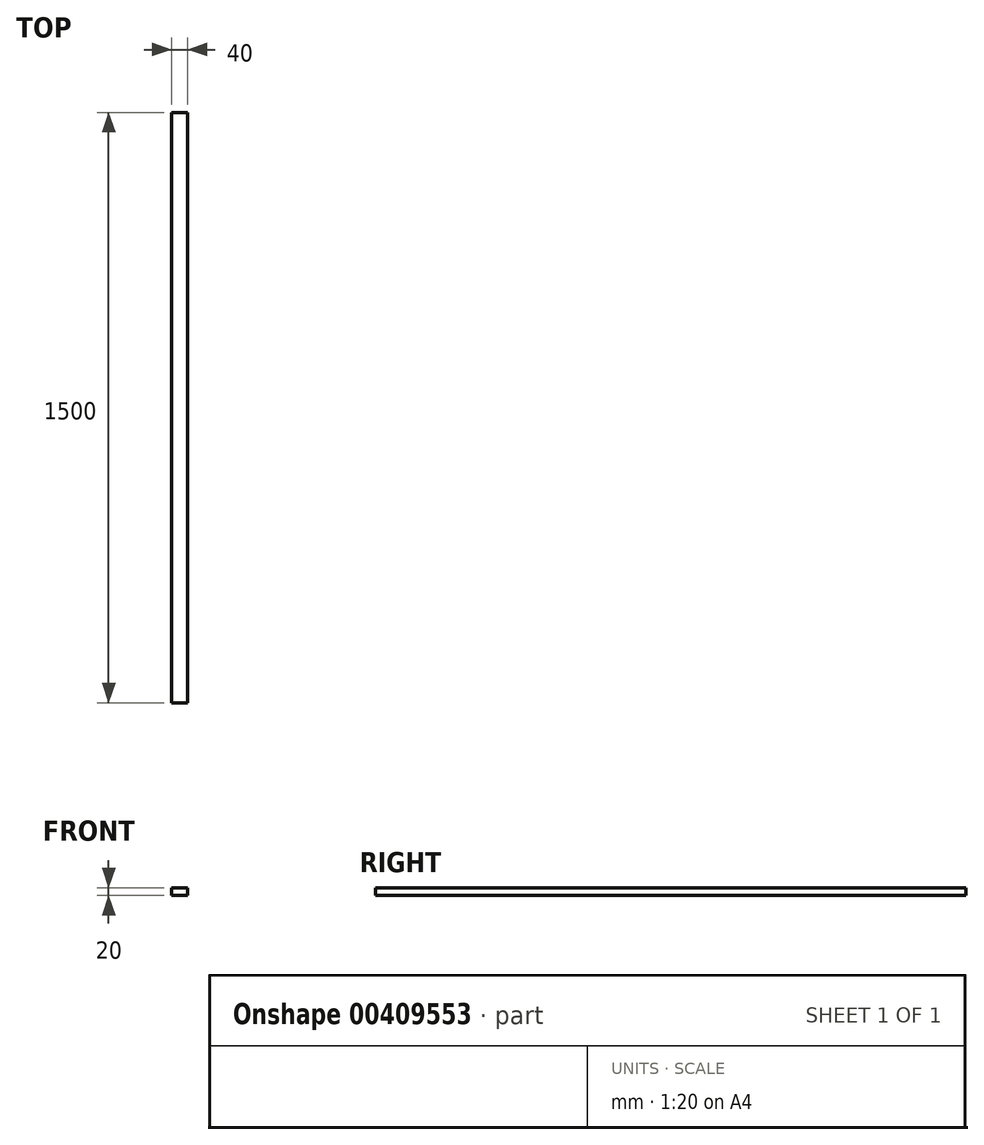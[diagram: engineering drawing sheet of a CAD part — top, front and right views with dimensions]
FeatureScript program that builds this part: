
annotation { "Feature Type Name" : "Feature", "Feature Type Description" : "" }
export const myFeature = defineFeature(function(context is Context, id is Id, definition is map)
    precondition{}
    {
        {
            var Q0;
            Q0=qCreatedBy(makeId("Front.planeOp"),FACE);
            var sketch = newSketch(context, id + "F0", { "sketchPlane" : qUnion([Q0])});
            skLineSegment(sketch, "E0.bottom", {"start": v(-24.83, 8.48) * mm, "end": v(15.17, 8.48) * mm});
            skLineSegment(sketch, "E0.top", {"start": v(-24.83, -11.52) * mm, "end": v(15.17, -11.52) * mm});
            skLineSegment(sketch, "E0.left", {"start": v(-24.83, 8.48) * mm, "end": v(-24.83, -11.52) * mm});
            skLineSegment(sketch, "E0.right", {"start": v(15.17, 8.48) * mm, "end": v(15.17, -11.52) * mm});
            skSolve(sketch);
        }
        {
            var Q0;
            Q0=makeQuery(id+"F0.imprint","IMPRINT",FACE,{"disambiguationData":[TD([[makeQuery(id+"F0.imprint","IMPRINT",EDGE,{"derivedFrom":sQuery(id+"F0.wireOp",EDGE,"E0.bottom")}),-1.0]])]});
            extrude(context, id + "F1", {"entities" : qUnion([Q0]), "depth" : 1500 * mm, "offsetDistance" : 25 * mm});
        }
    });
